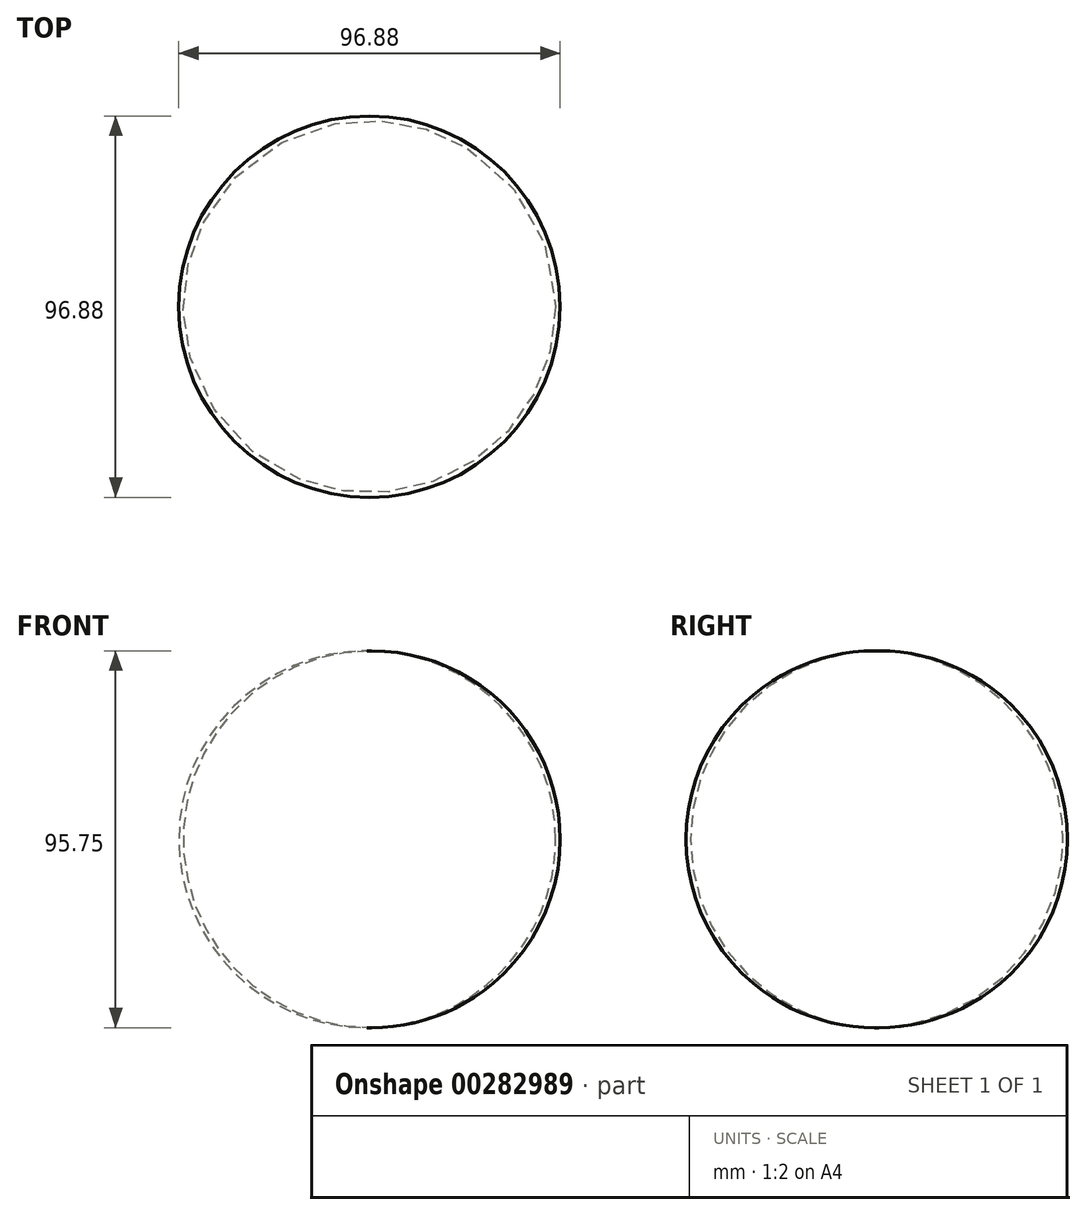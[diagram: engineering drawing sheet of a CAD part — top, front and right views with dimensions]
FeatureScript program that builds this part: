
annotation { "Feature Type Name" : "Feature", "Feature Type Description" : "" }
export const myFeature = defineFeature(function(context is Context, id is Id, definition is map)
    precondition{}
    {
        {
            var Q0;
            Q0=qCreatedBy(makeId("Front.planeOp"),FACE);
            var sketch = newSketch(context, id + "F0", { "sketchPlane" : qUnion([Q0])});
            skLineSegment(sketch, "E0", {"start": v(0, 76.57) * mm, "end": v(0, -75.42) * mm, "construction": true});
            skArc(sketch, "E1", {"start": v(0, -50.85) * mm, "mid": v(48.44, -2.98) * mm, "end": v(0, 44.88) * mm});
            skSolve(sketch);
        }
        {
            var Q0;
            Q0=sQuery(id+"F0.wireOp",EDGE,"E1");
            var Q1;
            Q1=sQuery(id+"F0.wireOp",EDGE,"E0");
            revolve(context, id + "F1", {"bodyType" : ToolBodyType.SURFACE, "surfaceEntities" : qUnion([Q0]), "axis" : qUnion([Q1]), "revolveType" : RevolveType.FULL});
        }
    });
